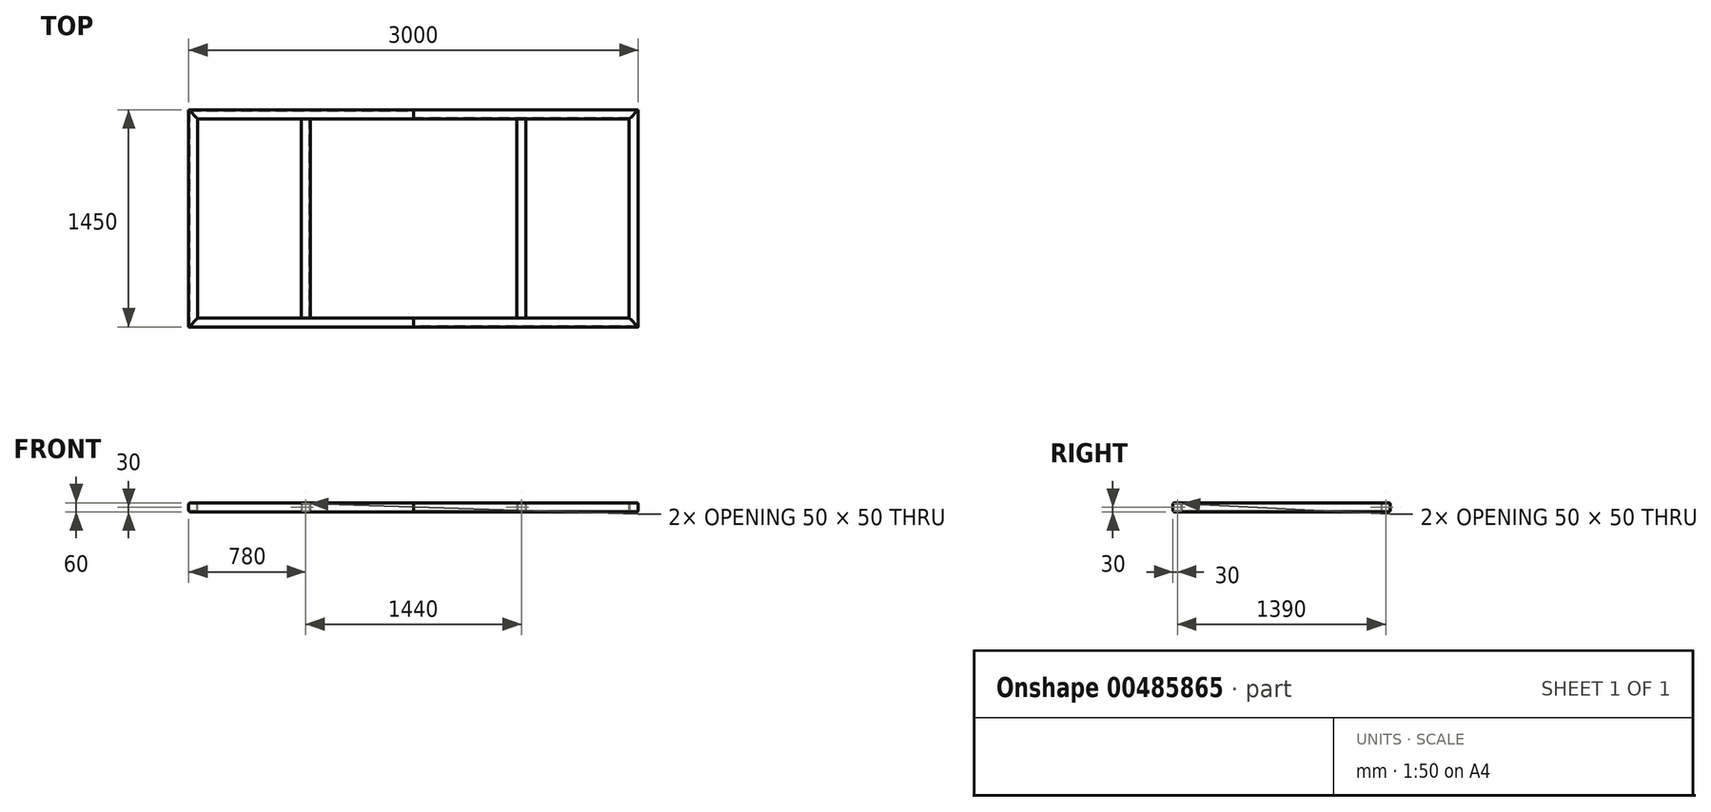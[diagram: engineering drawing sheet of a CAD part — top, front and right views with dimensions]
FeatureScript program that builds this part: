
annotation { "Feature Type Name" : "Feature", "Feature Type Description" : "" }
export const myFeature = defineFeature(function(context is Context, id is Id, definition is map)
    precondition{}
    {
        {
            var Q0;
            Q0=qCreatedBy(makeId("Right.planeOp"),FACE);
            var sketch = newSketch(context, id + "F0", { "sketchPlane" : qUnion([Q0])});
            skLineSegment(sketch, "E0.bottom", {"start": v(715, 30) * mm, "end": v(675, 30) * mm});
            skLineSegment(sketch, "E0.top", {"start": v(715, -30) * mm, "end": v(675, -30) * mm});
            skLineSegment(sketch, "E0.left", {"start": v(725, 20) * mm, "end": v(725, -20) * mm});
            skLineSegment(sketch, "E0.right", {"start": v(665, 20) * mm, "end": v(665, -20) * mm});
            skPoint(sketch, "E0.middle", {"position": v(695, 0) * mm});
            skPoint(sketch, "E1.visualSharp", {"position": v(665, 30) * mm});
            skArc(sketch, "E1.filletArc", {"start": v(675, 30) * mm, "mid": v(667.93, 27.07) * mm, "end": v(665, 20) * mm});
            skPoint(sketch, "E2.visualSharp", {"position": v(725, 30) * mm});
            skArc(sketch, "E2.filletArc", {"start": v(725, 20) * mm, "mid": v(722.07, 27.07) * mm, "end": v(715, 30) * mm});
            skPoint(sketch, "E3.visualSharp", {"position": v(725, -30) * mm});
            skArc(sketch, "E3.filletArc", {"start": v(715, -30) * mm, "mid": v(722.07, -27.07) * mm, "end": v(725, -20) * mm});
            skPoint(sketch, "E4.visualSharp", {"position": v(665, -30) * mm});
            skArc(sketch, "E4.filletArc", {"start": v(665, -20) * mm, "mid": v(667.93, -27.07) * mm, "end": v(675, -30) * mm});
            skArc(sketch, "E5.0", {"start": v(720, 20) * mm, "mid": v(718.54, 23.54) * mm, "end": v(715, 25) * mm});
            skLineSegment(sketch, "E5.1", {"start": v(720, 20) * mm, "end": v(720, -20) * mm});
            skLineSegment(sketch, "E5.2", {"start": v(715, 25) * mm, "end": v(675, 25) * mm});
            skArc(sketch, "E5.3", {"start": v(715, -25) * mm, "mid": v(718.54, -23.54) * mm, "end": v(720, -20) * mm});
            skArc(sketch, "E5.4", {"start": v(675, 25) * mm, "mid": v(671.46, 23.54) * mm, "end": v(670, 20) * mm});
            skLineSegment(sketch, "E5.5", {"start": v(670, 20) * mm, "end": v(670, -20) * mm});
            skArc(sketch, "E5.6", {"start": v(670, -20) * mm, "mid": v(671.46, -23.54) * mm, "end": v(675, -25) * mm});
            skLineSegment(sketch, "E5.7", {"start": v(715, -25) * mm, "end": v(675, -25) * mm});
            skSolve(sketch);
        }
        {
            var Q0;
            Q0 = qSketchRegion(id + "F0", true);
            extrude(context, id + "F1", {"entities" : qUnion([Q0]), "depth" : 1500 * mm});
        }
        {
            var Q0;
            Q0=makeQuery(id+"F1.opExtrude","SWEPT_FACE",FACE,{"disambiguationData":[OSD([sQuery(id+"F0.wireOp",EDGE,"E0.bottom")])]});
            var sketch = newSketch(context, id + "F2", { "sketchPlane" : qUnion([Q0])});
            skLineSegment(sketch, "E6", {"start": v(1500, 725) * mm, "end": v(1440, 665) * mm});
            skLineSegment(sketch, "E7", {"start": v(1440, 665) * mm, "end": v(1500, 665) * mm});
            skLineSegment(sketch, "E8", {"start": v(1500, 665) * mm, "end": v(1500, 725) * mm});
            skSolve(sketch);
        }
        {
            var Q0;
            Q0 = qSketchRegion(id + "F2", true);
            extrude(context, id + "F3", {"entities" : qUnion([Q0]), "operationType" : NewBodyOperationType.REMOVE, "endBound" : BoundingType.THROUGH_ALL, "oppositeDirection" : true, "depth" : 25 * mm});
        }
        {
            var Q0;
            Q0=qCreatedBy(makeId("Front.planeOp"),FACE);
            var sketch = newSketch(context, id + "F4", { "sketchPlane" : qUnion([Q0])});
            skLineSegment(sketch, "E9.0", {"start": v(1500, 20) * mm, "end": v(1500, -20) * mm});
            skArc(sketch, "E9.1", {"start": v(1490, 30) * mm, "mid": v(1497.07, 27.07) * mm, "end": v(1500, 20) * mm});
            skLineSegment(sketch, "E9.2", {"start": v(1490, 30) * mm, "end": v(1450, 30) * mm});
            skArc(sketch, "E9.3", {"start": v(1440, 20) * mm, "mid": v(1442.93, 27.07) * mm, "end": v(1450, 30) * mm});
            skLineSegment(sketch, "E9.4", {"start": v(1440, -20) * mm, "end": v(1440, 20) * mm});
            skArc(sketch, "E9.5", {"start": v(1450, -30) * mm, "mid": v(1442.93, -27.07) * mm, "end": v(1440, -20) * mm});
            skLineSegment(sketch, "E9.6", {"start": v(1450, -30) * mm, "end": v(1490, -30) * mm});
            skLineSegment(sketch, "E9.7", {"start": v(1450, -25) * mm, "end": v(1490, -25) * mm});
            skLineSegment(sketch, "E9.8", {"start": v(1445, -20) * mm, "end": v(1445, 20) * mm});
            skLineSegment(sketch, "E9.9", {"start": v(1450, 25) * mm, "end": v(1490, 25) * mm});
            skLineSegment(sketch, "E9.10", {"start": v(1495, -20) * mm, "end": v(1495, 20) * mm});
            skArc(sketch, "E9.11", {"start": v(1445, 20) * mm, "mid": v(1446.46, 23.54) * mm, "end": v(1450, 25) * mm});
            skArc(sketch, "E9.12", {"start": v(1450, -25) * mm, "mid": v(1446.46, -23.54) * mm, "end": v(1445, -20) * mm});
            skArc(sketch, "E9.13", {"start": v(1495, -20) * mm, "mid": v(1493.54, -23.54) * mm, "end": v(1490, -25) * mm});
            skArc(sketch, "E9.14", {"start": v(1490, 25) * mm, "mid": v(1493.54, 23.54) * mm, "end": v(1495, 20) * mm});
            skArc(sketch, "E9.15", {"start": v(1500, -20) * mm, "mid": v(1497.07, -27.07) * mm, "end": v(1490, -30) * mm});
            skSolve(sketch);
        }
        {
            var Q0;
            Q0 = qSketchRegion(id + "F4", true);
            extrude(context, id + "F5", {"entities" : qUnion([Q0]), "endBound" : BoundingType.UP_TO_NEXT, "oppositeDirection" : true, "depth" : 25 * mm});
        }
        {
            var Q0;
            Q0=makeQuery(id+"F5.opExtrude","SWEPT_BODY",BODY,{"disambiguationData":[OSD([sQuery(id+"F4.wireOp",EDGE,"E9.0"),sQuery(id+"F4.wireOp",EDGE,"E9.1"),sQuery(id+"F4.wireOp",EDGE,"E9.2"),sQuery(id+"F4.wireOp",EDGE,"E9.3"),sQuery(id+"F4.wireOp",EDGE,"E9.4"),sQuery(id+"F4.wireOp",EDGE,"E9.5"),sQuery(id+"F4.wireOp",EDGE,"E9.6"),sQuery(id+"F4.wireOp",EDGE,"E9.7"),sQuery(id+"F4.wireOp",EDGE,"E9.8"),sQuery(id+"F4.wireOp",EDGE,"E9.9"),sQuery(id+"F4.wireOp",EDGE,"E9.10"),sQuery(id+"F4.wireOp",EDGE,"E9.11"),sQuery(id+"F4.wireOp",EDGE,"E9.12"),sQuery(id+"F4.wireOp",EDGE,"E9.13"),sQuery(id+"F4.wireOp",EDGE,"E9.14"),sQuery(id+"F4.wireOp",EDGE,"E9.15")])]});
            var Q1;
            Q1=makeQuery(id+"F5.opExtrude","CAP_FACE",FACE,{"disambiguationData":[OSD([sQuery(id+"F4.wireOp",EDGE,"E9.0"),sQuery(id+"F4.wireOp",EDGE,"E9.1"),sQuery(id+"F4.wireOp",EDGE,"E9.2"),sQuery(id+"F4.wireOp",EDGE,"E9.3"),sQuery(id+"F4.wireOp",EDGE,"E9.4"),sQuery(id+"F4.wireOp",EDGE,"E9.5"),sQuery(id+"F4.wireOp",EDGE,"E9.6"),sQuery(id+"F4.wireOp",EDGE,"E9.7"),sQuery(id+"F4.wireOp",EDGE,"E9.8"),sQuery(id+"F4.wireOp",EDGE,"E9.9"),sQuery(id+"F4.wireOp",EDGE,"E9.10"),sQuery(id+"F4.wireOp",EDGE,"E9.11"),sQuery(id+"F4.wireOp",EDGE,"E9.12"),sQuery(id+"F4.wireOp",EDGE,"E9.13"),sQuery(id+"F4.wireOp",EDGE,"E9.14"),sQuery(id+"F4.wireOp",EDGE,"E9.15")])],"isStart":true});
            mirror(context, id + "F6", {"operationType" : NewBodyOperationType.ADD, "entities" : qUnion([Q0]), "mirrorPlane" : qUnion([Q1])});
        }
        {
            var Q0;
            Q0=makeQuery(id+"F1.opExtrude","SWEPT_BODY",BODY,{"disambiguationData":[OSD([sQuery(id+"F0.wireOp",EDGE,"E0.bottom"),sQuery(id+"F0.wireOp",EDGE,"E0.top"),sQuery(id+"F0.wireOp",EDGE,"E0.left"),sQuery(id+"F0.wireOp",EDGE,"E0.right"),sQuery(id+"F0.wireOp",EDGE,"E1.filletArc"),sQuery(id+"F0.wireOp",EDGE,"E2.filletArc"),sQuery(id+"F0.wireOp",EDGE,"E3.filletArc"),sQuery(id+"F0.wireOp",EDGE,"E4.filletArc"),sQuery(id+"F0.wireOp",EDGE,"E5.0"),sQuery(id+"F0.wireOp",EDGE,"E5.1"),sQuery(id+"F0.wireOp",EDGE,"E5.2"),sQuery(id+"F0.wireOp",EDGE,"E5.3"),sQuery(id+"F0.wireOp",EDGE,"E5.4"),sQuery(id+"F0.wireOp",EDGE,"E5.5"),sQuery(id+"F0.wireOp",EDGE,"E5.6"),sQuery(id+"F0.wireOp",EDGE,"E5.7")])]});
            var Q1;
            Q1=qCreatedBy(makeId("Front.planeOp"),FACE);
            mirror(context, id + "F7", {"entities" : qUnion([Q0]), "mirrorPlane" : qUnion([Q1])});
        }
        {
            var Q0;
            Q0=makeQuery(id+"F1.opExtrude","SWEPT_FACE",FACE,{"disambiguationData":[OSD([sQuery(id+"F0.wireOp",EDGE,"E0.right")])]});
            var sketch = newSketch(context, id + "F8", { "sketchPlane" : qUnion([Q0])});
            skLineSegment(sketch, "E10.bottom", {"start": v(740, 30) * mm, "end": v(700, 30) * mm});
            skLineSegment(sketch, "E10.top", {"start": v(740, -30) * mm, "end": v(700, -30) * mm});
            skLineSegment(sketch, "E10.left", {"start": v(750, 20) * mm, "end": v(750, -20) * mm});
            skLineSegment(sketch, "E10.right", {"start": v(690, 20) * mm, "end": v(690, -20) * mm});
            skPoint(sketch, "E10.middle", {"position": v(720, 0) * mm});
            skPoint(sketch, "E11.visualSharp", {"position": v(690, 30) * mm});
            skArc(sketch, "E11.filletArc", {"start": v(700, 30) * mm, "mid": v(692.93, 27.07) * mm, "end": v(690, 20) * mm});
            skPoint(sketch, "E12.visualSharp", {"position": v(750, 30) * mm});
            skArc(sketch, "E12.filletArc", {"start": v(750, 20) * mm, "mid": v(747.07, 27.07) * mm, "end": v(740, 30) * mm});
            skPoint(sketch, "E13.visualSharp", {"position": v(750, -30) * mm});
            skArc(sketch, "E13.filletArc", {"start": v(740, -30) * mm, "mid": v(747.07, -27.07) * mm, "end": v(750, -20) * mm});
            skPoint(sketch, "E14.visualSharp", {"position": v(690, -30) * mm});
            skArc(sketch, "E14.filletArc", {"start": v(690, -20) * mm, "mid": v(692.93, -27.07) * mm, "end": v(700, -30) * mm});
            skArc(sketch, "E15.0", {"start": v(745, 20) * mm, "mid": v(743.54, 23.54) * mm, "end": v(740, 25) * mm});
            skLineSegment(sketch, "E15.1", {"start": v(745, 20) * mm, "end": v(745, -20) * mm});
            skLineSegment(sketch, "E15.2", {"start": v(740, 25) * mm, "end": v(700, 25) * mm});
            skArc(sketch, "E15.3", {"start": v(740, -25) * mm, "mid": v(743.54, -23.54) * mm, "end": v(745, -20) * mm});
            skArc(sketch, "E15.4", {"start": v(700, 25) * mm, "mid": v(696.46, 23.54) * mm, "end": v(695, 20) * mm});
            skLineSegment(sketch, "E15.5", {"start": v(695, 20) * mm, "end": v(695, -20) * mm});
            skArc(sketch, "E15.6", {"start": v(695, -20) * mm, "mid": v(696.46, -23.54) * mm, "end": v(700, -25) * mm});
            skLineSegment(sketch, "E15.7", {"start": v(740, -25) * mm, "end": v(700, -25) * mm});
            skLineSegment(sketch, "E16.direction1", {"start": v(690, -30) * mm, "end": v(470, -30) * mm, "construction": true});
            skSolve(sketch);
        }
        {
            var Q0;
            Q0 = qSketchRegion(id + "F8", true);
            var Q1;
            Q1=makeQuery(id+"F7.opPattern","COPY",FACE,{"derivedFrom":makeQuery(id+"F1.opExtrude","SWEPT_FACE",FACE,{"disambiguationData":[OSD([sQuery(id+"F0.wireOp",EDGE,"E0.right")])]}),"instanceName":"1"});
            extrude(context, id + "F9", {"entities" : qUnion([Q0]), "endBound" : BoundingType.UP_TO_SURFACE, "endBoundEntityFace" : qUnion([Q1]), "depth" : 25 * mm});
        }
        {
            var Q0;
            Q0=makeQuery(id+"F1.opExtrude","SWEPT_BODY",BODY,{"disambiguationData":[OSD([sQuery(id+"F0.wireOp",EDGE,"E0.bottom"),sQuery(id+"F0.wireOp",EDGE,"E0.top"),sQuery(id+"F0.wireOp",EDGE,"E0.left"),sQuery(id+"F0.wireOp",EDGE,"E0.right"),sQuery(id+"F0.wireOp",EDGE,"E1.filletArc"),sQuery(id+"F0.wireOp",EDGE,"E2.filletArc"),sQuery(id+"F0.wireOp",EDGE,"E3.filletArc"),sQuery(id+"F0.wireOp",EDGE,"E4.filletArc"),sQuery(id+"F0.wireOp",EDGE,"E5.0"),sQuery(id+"F0.wireOp",EDGE,"E5.1"),sQuery(id+"F0.wireOp",EDGE,"E5.2"),sQuery(id+"F0.wireOp",EDGE,"E5.3"),sQuery(id+"F0.wireOp",EDGE,"E5.4"),sQuery(id+"F0.wireOp",EDGE,"E5.5"),sQuery(id+"F0.wireOp",EDGE,"E5.6"),sQuery(id+"F0.wireOp",EDGE,"E5.7")])]});
            var Q1;
            Q1=makeQuery(id+"F5.opExtrude","SWEPT_BODY",BODY,{"disambiguationData":[OSD([sQuery(id+"F4.wireOp",EDGE,"E9.0"),sQuery(id+"F4.wireOp",EDGE,"E9.1"),sQuery(id+"F4.wireOp",EDGE,"E9.2"),sQuery(id+"F4.wireOp",EDGE,"E9.3"),sQuery(id+"F4.wireOp",EDGE,"E9.4"),sQuery(id+"F4.wireOp",EDGE,"E9.5"),sQuery(id+"F4.wireOp",EDGE,"E9.6"),sQuery(id+"F4.wireOp",EDGE,"E9.7"),sQuery(id+"F4.wireOp",EDGE,"E9.8"),sQuery(id+"F4.wireOp",EDGE,"E9.9"),sQuery(id+"F4.wireOp",EDGE,"E9.10"),sQuery(id+"F4.wireOp",EDGE,"E9.11"),sQuery(id+"F4.wireOp",EDGE,"E9.12"),sQuery(id+"F4.wireOp",EDGE,"E9.13"),sQuery(id+"F4.wireOp",EDGE,"E9.14"),sQuery(id+"F4.wireOp",EDGE,"E9.15")])]});
            var Q2;
            Q2=makeQuery(id+"F7.opPattern","COPY",BODY,{"derivedFrom":makeQuery(id+"F1.opExtrude","SWEPT_BODY",BODY,{"disambiguationData":[OSD([sQuery(id+"F0.wireOp",EDGE,"E0.bottom"),sQuery(id+"F0.wireOp",EDGE,"E0.top"),sQuery(id+"F0.wireOp",EDGE,"E0.left"),sQuery(id+"F0.wireOp",EDGE,"E0.right"),sQuery(id+"F0.wireOp",EDGE,"E1.filletArc"),sQuery(id+"F0.wireOp",EDGE,"E2.filletArc"),sQuery(id+"F0.wireOp",EDGE,"E3.filletArc"),sQuery(id+"F0.wireOp",EDGE,"E4.filletArc"),sQuery(id+"F0.wireOp",EDGE,"E5.0"),sQuery(id+"F0.wireOp",EDGE,"E5.1"),sQuery(id+"F0.wireOp",EDGE,"E5.2"),sQuery(id+"F0.wireOp",EDGE,"E5.3"),sQuery(id+"F0.wireOp",EDGE,"E5.4"),sQuery(id+"F0.wireOp",EDGE,"E5.5"),sQuery(id+"F0.wireOp",EDGE,"E5.6"),sQuery(id+"F0.wireOp",EDGE,"E5.7")])]}),"instanceName":"1"});
            var Q3;
            Q3=makeQuery(id+"F9.opExtrude","SWEPT_BODY",BODY,{"disambiguationData":[OSD([sQuery(id+"F8.wireOp",EDGE,"E16.1.0.1"),sQuery(id+"F8.wireOp",EDGE,"E16.1.0.2"),sQuery(id+"F8.wireOp",EDGE,"E16.1.0.4"),sQuery(id+"F8.wireOp",EDGE,"E16.1.0.7"),sQuery(id+"F8.wireOp",EDGE,"E16.1.0.9"),sQuery(id+"F8.wireOp",EDGE,"E16.1.0.10"),sQuery(id+"F8.wireOp",EDGE,"E16.1.0.11"),sQuery(id+"F8.wireOp",EDGE,"E16.1.0.12"),sQuery(id+"F8.wireOp",EDGE,"E16.1.0.13"),sQuery(id+"F8.wireOp",EDGE,"E16.1.0.14"),sQuery(id+"F8.wireOp",EDGE,"E16.1.0.15"),sQuery(id+"F8.wireOp",EDGE,"E16.1.0.16"),sQuery(id+"F8.wireOp",EDGE,"E16.1.0.17"),sQuery(id+"F8.wireOp",EDGE,"E16.1.0.18"),sQuery(id+"F8.wireOp",EDGE,"E16.1.0.19"),sQuery(id+"F8.wireOp",EDGE,"E16.1.0.20")])]});
            var Q4;
            Q4=makeQuery(id+"F9.opExtrude","SWEPT_BODY",BODY,{"disambiguationData":[OSD([sQuery(id+"F8.wireOp",EDGE,"E10.bottom"),sQuery(id+"F8.wireOp",EDGE,"E10.top"),sQuery(id+"F8.wireOp",EDGE,"E10.left"),sQuery(id+"F8.wireOp",EDGE,"E10.right"),sQuery(id+"F8.wireOp",EDGE,"E11.filletArc"),sQuery(id+"F8.wireOp",EDGE,"E12.filletArc"),sQuery(id+"F8.wireOp",EDGE,"E13.filletArc"),sQuery(id+"F8.wireOp",EDGE,"E14.filletArc"),sQuery(id+"F8.wireOp",EDGE,"E15.0"),sQuery(id+"F8.wireOp",EDGE,"E15.1"),sQuery(id+"F8.wireOp",EDGE,"E15.2"),sQuery(id+"F8.wireOp",EDGE,"E15.3"),sQuery(id+"F8.wireOp",EDGE,"E15.4"),sQuery(id+"F8.wireOp",EDGE,"E15.5"),sQuery(id+"F8.wireOp",EDGE,"E15.6"),sQuery(id+"F8.wireOp",EDGE,"E15.7")])]});
            var Q5;
            Q5=makeQuery(id+"F1.opExtrude","CAP_FACE",FACE,{"disambiguationData":[OSD([sQuery(id+"F0.wireOp",EDGE,"E0.bottom"),sQuery(id+"F0.wireOp",EDGE,"E0.top"),sQuery(id+"F0.wireOp",EDGE,"E0.left"),sQuery(id+"F0.wireOp",EDGE,"E0.right"),sQuery(id+"F0.wireOp",EDGE,"E1.filletArc"),sQuery(id+"F0.wireOp",EDGE,"E2.filletArc"),sQuery(id+"F0.wireOp",EDGE,"E3.filletArc"),sQuery(id+"F0.wireOp",EDGE,"E4.filletArc"),sQuery(id+"F0.wireOp",EDGE,"E5.0"),sQuery(id+"F0.wireOp",EDGE,"E5.1"),sQuery(id+"F0.wireOp",EDGE,"E5.2"),sQuery(id+"F0.wireOp",EDGE,"E5.3"),sQuery(id+"F0.wireOp",EDGE,"E5.4"),sQuery(id+"F0.wireOp",EDGE,"E5.5"),sQuery(id+"F0.wireOp",EDGE,"E5.6"),sQuery(id+"F0.wireOp",EDGE,"E5.7")])],"isStart":true});
            mirror(context, id + "F10", {"entities" : qUnion([Q0, Q1, Q2, Q3, Q4]), "mirrorPlane" : qUnion([Q5])});
        }
    });
